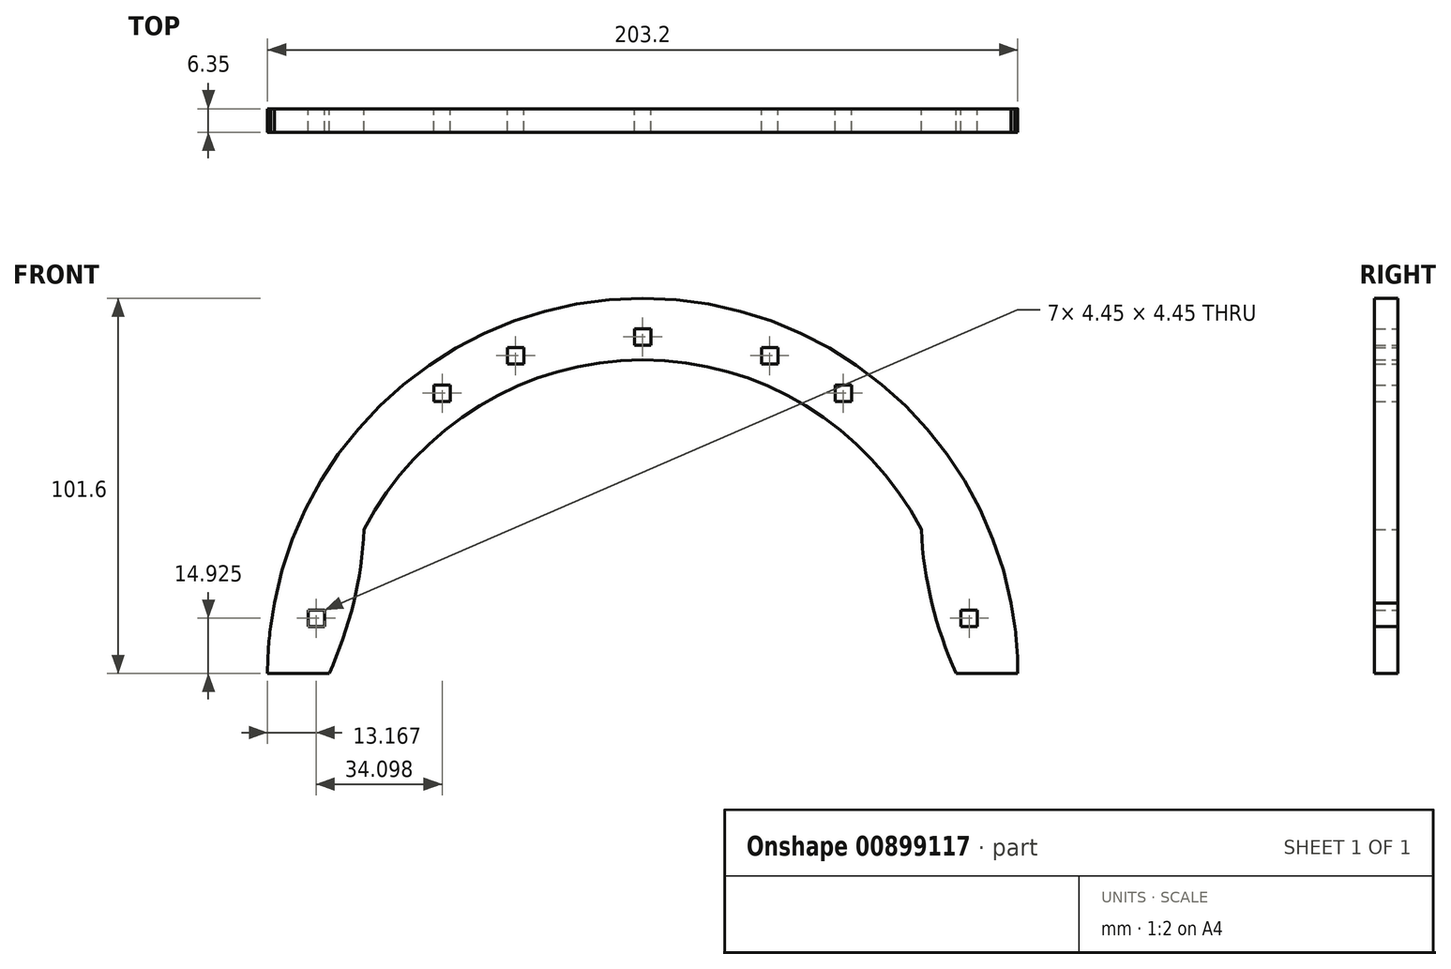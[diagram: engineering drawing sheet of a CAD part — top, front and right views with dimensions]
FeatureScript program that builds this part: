
annotation { "Feature Type Name" : "Feature", "Feature Type Description" : "" }
export const myFeature = defineFeature(function(context is Context, id is Id, definition is map)
    precondition{}
    {
        {
            var Q0;
            Q0=qCreatedBy(makeId("Front.planeOp"),FACE);
            var sketch = newSketch(context, id + "F0", { "sketchPlane" : qUnion([Q0])});
            skLineSegment(sketch, "E0", {"start": v(84.93, 0) * mm, "end": v(101.6, 0) * mm});
            skLineSegment(sketch, "E1.MirrorCS", {"start": v(-84.93, 0) * mm, "end": v(-101.6, 0) * mm});
            skArc(sketch, "E2", {"start": v(101.6, 0) * mm, "mid": v(101.4, 6.36) * mm, "end": v(100.8, 12.7) * mm});
            skArc(sketch, "E3.trimOffspring", {"start": v(-100.8, 12.7) * mm, "mid": v(-101.4, 6.36) * mm, "end": v(-101.6, 0) * mm});
            skArc(sketch, "E4.trimOffspring", {"start": v(99.8, 19.05) * mm, "mid": v(0, 101.6) * mm, "end": v(-99.8, 19.05) * mm});
            skLineSegment(sketch, "E5.bottom", {"start": v(2.22, 88.9) * mm, "end": v(-2.23, 88.9) * mm});
            skLineSegment(sketch, "E5.top", {"start": v(2.22, 93.35) * mm, "end": v(-2.23, 93.35) * mm});
            skLineSegment(sketch, "E5.left", {"start": v(2.22, 88.9) * mm, "end": v(2.22, 93.35) * mm});
            skLineSegment(sketch, "E5.right", {"start": v(-2.23, 88.9) * mm, "end": v(-2.23, 93.35) * mm});
            skPoint(sketch, "E5.middle", {"position": v(0, 91.12) * mm});
            skLineSegment(sketch, "E6.bottom", {"start": v(-52.11, 73.66) * mm, "end": v(-56.56, 73.66) * mm});
            skLineSegment(sketch, "E6.top", {"start": v(-52.11, 78.11) * mm, "end": v(-56.56, 78.11) * mm});
            skLineSegment(sketch, "E6.left", {"start": v(-52.11, 73.66) * mm, "end": v(-52.11, 78.11) * mm});
            skLineSegment(sketch, "E6.right", {"start": v(-56.56, 73.66) * mm, "end": v(-56.56, 78.11) * mm});
            skPoint(sketch, "E6.middle", {"position": v(-54.34, 75.89) * mm});
            skLineSegment(sketch, "E7.MirrorCS", {"start": v(52.11, 73.66) * mm, "end": v(56.56, 73.66) * mm});
            skLineSegment(sketch, "E8.MirrorCS", {"start": v(52.11, 78.11) * mm, "end": v(56.56, 78.11) * mm});
            skLineSegment(sketch, "E9.MirrorCS", {"start": v(56.56, 73.66) * mm, "end": v(56.56, 78.11) * mm});
            skLineSegment(sketch, "E10.MirrorCS", {"start": v(52.11, 73.66) * mm, "end": v(52.11, 78.11) * mm});
            skLineSegment(sketch, "E11.bottom", {"start": v(-32.18, 83.82) * mm, "end": v(-36.63, 83.82) * mm});
            skLineSegment(sketch, "E11.top", {"start": v(-32.18, 88.27) * mm, "end": v(-36.63, 88.27) * mm});
            skLineSegment(sketch, "E11.left", {"start": v(-32.18, 83.82) * mm, "end": v(-32.18, 88.27) * mm});
            skLineSegment(sketch, "E11.right", {"start": v(-36.63, 83.82) * mm, "end": v(-36.63, 88.27) * mm});
            skPoint(sketch, "E11.middle", {"position": v(-34.4, 86.05) * mm});
            skLineSegment(sketch, "E12.MirrorCS", {"start": v(32.18, 83.82) * mm, "end": v(32.18, 88.27) * mm});
            skLineSegment(sketch, "E13.MirrorCS", {"start": v(32.18, 83.82) * mm, "end": v(36.63, 83.82) * mm});
            skLineSegment(sketch, "E14.MirrorCS", {"start": v(36.63, 83.82) * mm, "end": v(36.63, 88.27) * mm});
            skLineSegment(sketch, "E15.MirrorCS", {"start": v(32.18, 88.27) * mm, "end": v(36.63, 88.27) * mm});
            skLineSegment(sketch, "E16.MirrorCS", {"start": v(-85.73, 12.7) * mm, "end": v(-90.66, 12.7) * mm});
            skLineSegment(sketch, "E17", {"start": v(-85.73, 12.7) * mm, "end": v(-83.97, 12.7) * mm});
            skLineSegment(sketch, "E18", {"start": v(-99.8, 19.05) * mm, "end": v(-100.8, 12.7) * mm});
            skPoint(sketch, "E19.right.end.orphan", {"position": v(-95.87, 19.05) * mm});
            skPoint(sketch, "E19.right.start.orphan", {"position": v(-95.87, 12.7) * mm});
            skLineSegment(sketch, "E20", {"start": v(99.8, 19.05) * mm, "end": v(100.8, 12.7) * mm});
            skArc(sketch, "E21.trimOffspring", {"start": v(75.46, 38.97) * mm, "mid": v(0, 84.93) * mm, "end": v(-75.46, 38.97) * mm});
            skArc(sketch, "E22", {"start": v(-84.93, 0) * mm, "mid": v(-78.33, 19.03) * mm, "end": v(-75.46, 38.97) * mm});
            skArc(sketch, "E23.MirrorCS", {"start": v(84.93, 0) * mm, "mid": v(78.33, 19.03) * mm, "end": v(75.46, 38.97) * mm});
            skLineSegment(sketch, "E24.bottom", {"start": v(-90.66, 12.7) * mm, "end": v(-86.2, 12.7) * mm});
            skLineSegment(sketch, "E24.top", {"start": v(-90.66, 17.15) * mm, "end": v(-86.2, 17.15) * mm});
            skLineSegment(sketch, "E24.left", {"start": v(-90.66, 12.7) * mm, "end": v(-90.66, 17.15) * mm});
            skLineSegment(sketch, "E24.right", {"start": v(-86.2, 12.7) * mm, "end": v(-86.2, 17.15) * mm});
            skLineSegment(sketch, "E25.MirrorCS", {"start": v(90.66, 12.7) * mm, "end": v(86.2, 12.7) * mm});
            skLineSegment(sketch, "E26.MirrorCS", {"start": v(86.2, 12.7) * mm, "end": v(86.2, 17.15) * mm});
            skLineSegment(sketch, "E27.MirrorCS", {"start": v(90.66, 17.15) * mm, "end": v(86.2, 17.15) * mm});
            skLineSegment(sketch, "E28.MirrorCS", {"start": v(90.66, 12.7) * mm, "end": v(90.66, 17.15) * mm});
            skSolve(sketch);
        }
        {
            var Q0;
            Q0=makeQuery(id+"F0.imprint","IMPRINT",FACE,{"disambiguationData":[TD([[makeQuery(id+"F0.imprint","IMPRINT",EDGE,{"derivedFrom":sQuery(id+"F0.wireOp",EDGE,"E0")}),1.0]])]});
            extrude(context, id + "F1", {"entities" : qUnion([Q0]), "depth" : 6.35 * mm, "offsetDistance" : 25 * mm});
        }
    });
